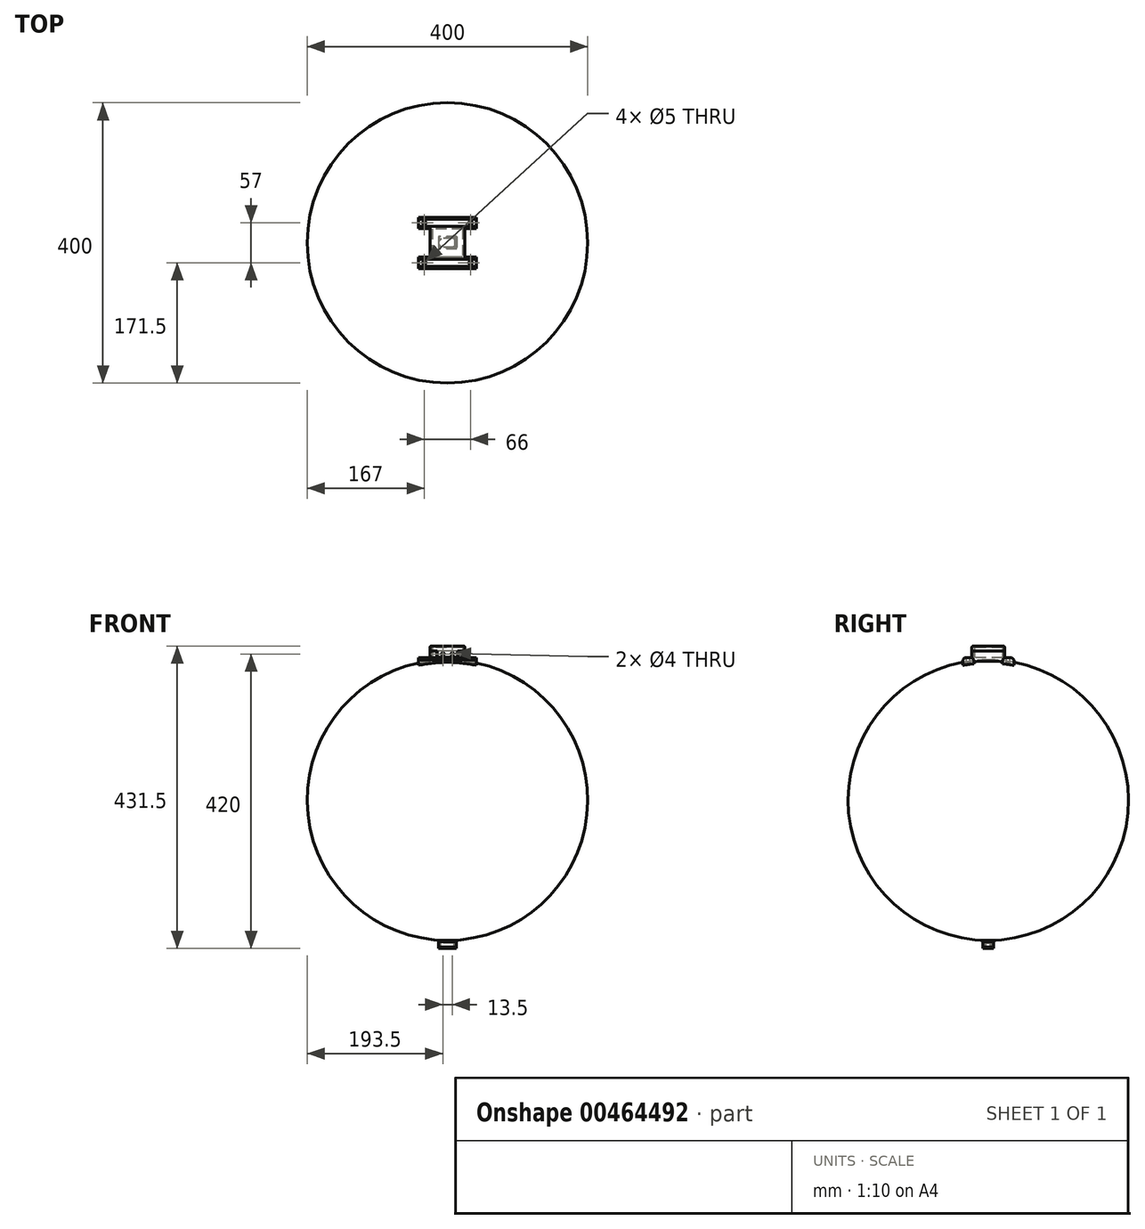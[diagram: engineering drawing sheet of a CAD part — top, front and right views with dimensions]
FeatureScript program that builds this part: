
annotation { "Feature Type Name" : "Feature", "Feature Type Description" : "" }
export const myFeature = defineFeature(function(context is Context, id is Id, definition is map)
    precondition{}
    {
        {
            assignVariable(context, id + "F0", {"name" : "R", "anyValue" : 200});
        }
        {
            assignVariable(context, id + "F1", {"name" : "T", "anyValue" : 3});
        }
        {
            assignVariable(context, id + "F2", {"name" : "t", "anyValue" : 2});
        }
        {
            var Q0;
            Q0=qCreatedBy(makeId("Right.planeOp"),FACE);
            var sketch = newSketch(context, id + "F3", { "sketchPlane" : qUnion([Q0])});
            skArc(sketch, "E0", {"start": v(0, -200) * mm, "mid": v(200, 0) * mm, "end": v(0, 200) * mm});
            skLineSegment(sketch, "E1", {"start": v(0, 133.29) * mm, "end": v(0, -166.2) * mm, "construction": true});
            skLineSegment(sketch, "E2", {"start": v(0, 200) * mm, "end": v(0, -200) * mm});
            skSolve(sketch);
        }
        {
            var Q0;
            Q0=makeQuery(id+"F3.imprint","IMPRINT",FACE,{"disambiguationData":[TD([[makeQuery(id+"F3.imprint","IMPRINT",EDGE,{"derivedFrom":sQuery(id+"F3.wireOp",EDGE,"E0")}),1.0]])]});
            var Q1;
            Q1=sQuery(id+"F3.wireOp",EDGE,"E1");
            revolve(context, id + "F4", {"entities" : qUnion([Q0]), "axis" : qUnion([Q1]), "revolveType" : RevolveType.FULL});
        }
        {
            var Q0;
            Q0=qCreatedBy(makeId("Top.planeOp"),FACE);
            cPlane(context, id + "F5", {"entities" : qUnion([Q0]), "cplaneType" : CPlaneType.OFFSET, "offset" : (getVariable(context, 'R') + getVariable(context, 'T')) * mm, "width" : 150 * mm, "height" : 150 * mm});
        }
        {
            var Q0;
            Q0=qCreatedBy(id+"F5.planeOp",FACE);
            var sketch = newSketch(context, id + "F6", { "sketchPlane" : qUnion([Q0])});
            skLineSegment(sketch, "E3.bottom", {"start": v(25, 36.5) * mm, "end": v(-25, 36.5) * mm});
            skLineSegment(sketch, "E3.top", {"start": v(25, -36.5) * mm, "end": v(-25, -36.5) * mm});
            skLineSegment(sketch, "E3.left", {"start": v(25, 20.5) * mm, "end": v(25, -20.5) * mm});
            skLineSegment(sketch, "E3.right", {"start": v(-25, 20.5) * mm, "end": v(-25, -20.5) * mm});
            skPoint(sketch, "E3.middle", {"position": v(0, 0) * mm});
            skLineSegment(sketch, "E4.bottom", {"start": v(-25, 36.5) * mm, "end": v(-41, 36.5) * mm});
            skLineSegment(sketch, "E4.top", {"start": v(-25, 20.5) * mm, "end": v(-41, 20.5) * mm});
            skLineSegment(sketch, "E4.right", {"start": v(-41, 36.5) * mm, "end": v(-41, 20.5) * mm});
            skLineSegment(sketch, "E5", {"start": v(0, 40.93) * mm, "end": v(0, -41.3) * mm, "construction": true});
            skLineSegment(sketch, "E6", {"start": v(40.69, 0) * mm, "end": v(-40.56, 0) * mm, "construction": true});
            skLineSegment(sketch, "E7.MirrorCS", {"start": v(25, 20.5) * mm, "end": v(41, 20.5) * mm});
            skLineSegment(sketch, "E8.MirrorCS", {"start": v(41, 36.5) * mm, "end": v(41, 20.5) * mm});
            skLineSegment(sketch, "E9.MirrorCS", {"start": v(25, 36.5) * mm, "end": v(41, 36.5) * mm});
            skLineSegment(sketch, "E10.MirrorCS", {"start": v(-25, -20.5) * mm, "end": v(-41, -20.5) * mm});
            skLineSegment(sketch, "E11.MirrorCS", {"start": v(-41, -36.5) * mm, "end": v(-41, -20.5) * mm});
            skLineSegment(sketch, "E12.MirrorCS", {"start": v(-25, -36.5) * mm, "end": v(-41, -36.5) * mm});
            skLineSegment(sketch, "E13.MirrorCS", {"start": v(25, -36.5) * mm, "end": v(41, -36.5) * mm});
            skLineSegment(sketch, "E14.MirrorCS", {"start": v(41, -36.5) * mm, "end": v(41, -20.5) * mm});
            skLineSegment(sketch, "E15.MirrorCS", {"start": v(25, -20.5) * mm, "end": v(41, -20.5) * mm});
            skLineSegment(sketch, "E16", {"start": v(-25, 20.5) * mm, "end": v(-41, 36.5) * mm, "construction": true});
            skLineSegment(sketch, "E17", {"start": v(-25, 36.5) * mm, "end": v(-41, 20.5) * mm, "construction": true});
            skCircle(sketch, "E18", {"center": v(-33, 28.5) * mm, "radius": 2.5 * mm});
            skCircle(sketch, "E19.MirrorC", {"center": v(33, 28.5) * mm, "radius": 2.5 * mm});
            skCircle(sketch, "E20.MirrorC", {"center": v(-33, -28.5) * mm, "radius": 2.5 * mm});
            skCircle(sketch, "E21.MirrorC", {"center": v(33, -28.5) * mm, "radius": 2.5 * mm});
            skSolve(sketch);
        }
        {
            var Q0;
            Q0 = qSketchRegion(id + "F6", true);
            var Q1;
            Q1=makeQuery(id+"F4.opRevolve","SWEPT_FACE",FACE,{"disambiguationData":[OSD([sQuery(id+"F3.wireOp",EDGE,"E0")])]});
            extrude(context, id + "F7", {"entities" : qUnion([Q0]), "endBound" : BoundingType.UP_TO_SURFACE, "oppositeDirection" : true, "depth" : 25 * mm, "endBoundEntityFace" : qUnion([Q1]), "offsetDistance" : 25 * mm});
        }
        {
            var Q0;
            Q0=makeQuery(id+"F7.opExtrude","CAP_EDGE",EDGE,{"disambiguationData":[OSD([sQuery(id+"F6.wireOp",EDGE,"E3.bottom"),sQuery(id+"F6.wireOp",EDGE,"E4.bottom"),sQuery(id+"F6.wireOp",EDGE,"E9.MirrorCS")])],"isStart":true});
            var Q1;
            Q1=makeQuery(id+"F7.opExtrude","CAP_EDGE",EDGE,{"disambiguationData":[OSD([sQuery(id+"F6.wireOp",EDGE,"E3.top"),sQuery(id+"F6.wireOp",EDGE,"E12.MirrorCS"),sQuery(id+"F6.wireOp",EDGE,"E13.MirrorCS")])],"isStart":true});
            var Q2;
            Q2=makeQuery(id+"F7.opExtrude","CAP_EDGE",EDGE,{"disambiguationData":[OSD([sQuery(id+"F6.wireOp",EDGE,"E4.top")])],"isStart":true});
            var Q3;
            Q3=makeQuery(id+"F7.opExtrude","CAP_EDGE",EDGE,{"disambiguationData":[OSD([sQuery(id+"F6.wireOp",EDGE,"E7.MirrorCS")])],"isStart":true});
            var Q4;
            Q4=makeQuery(id+"F7.opExtrude","CAP_EDGE",EDGE,{"disambiguationData":[OSD([sQuery(id+"F6.wireOp",EDGE,"E15.MirrorCS")])],"isStart":true});
            var Q5;
            Q5=makeQuery(id+"F7.opExtrude","CAP_EDGE",EDGE,{"disambiguationData":[OSD([sQuery(id+"F6.wireOp",EDGE,"E10.MirrorCS")])],"isStart":true});
            chamfer(context, id + "F8", {"entities" : qUnion([Q0, Q1, Q2, Q3, Q4, Q5]), "width" : 3 * mm, "tangentPropagation" : true});
        }
        {
            var Q0;
            Q0=makeQuery(id+"F7.opExtrude","CAP_FACE",FACE,{"disambiguationData":[OSD([sQuery(id+"F6.wireOp",EDGE,"E3.bottom"),sQuery(id+"F6.wireOp",EDGE,"E3.top"),sQuery(id+"F6.wireOp",EDGE,"E3.left"),sQuery(id+"F6.wireOp",EDGE,"E3.right"),sQuery(id+"F6.wireOp",EDGE,"E4.bottom"),sQuery(id+"F6.wireOp",EDGE,"E4.top"),sQuery(id+"F6.wireOp",EDGE,"E4.right"),sQuery(id+"F6.wireOp",EDGE,"E7.MirrorCS"),sQuery(id+"F6.wireOp",EDGE,"E8.MirrorCS"),sQuery(id+"F6.wireOp",EDGE,"E9.MirrorCS"),sQuery(id+"F6.wireOp",EDGE,"E10.MirrorCS"),sQuery(id+"F6.wireOp",EDGE,"E11.MirrorCS"),sQuery(id+"F6.wireOp",EDGE,"E12.MirrorCS"),sQuery(id+"F6.wireOp",EDGE,"E13.MirrorCS"),sQuery(id+"F6.wireOp",EDGE,"E14.MirrorCS"),sQuery(id+"F6.wireOp",EDGE,"E15.MirrorCS"),sQuery(id+"F6.wireOp",EDGE,"E18"),sQuery(id+"F6.wireOp",EDGE,"E19.MirrorC"),sQuery(id+"F6.wireOp",EDGE,"E20.MirrorC"),sQuery(id+"F6.wireOp",EDGE,"E21.MirrorC")])],"isStart":true});
            var sketch = newSketch(context, id + "F9", { "sketchPlane" : qUnion([Q0])});
            skLineSegment(sketch, "E22.bottom", {"start": v(25, 23.5) * mm, "end": v(-25, 23.5) * mm});
            skLineSegment(sketch, "E22.top", {"start": v(25, -23.5) * mm, "end": v(15, -23.5) * mm});
            skLineSegment(sketch, "E22.left", {"start": v(25, 23.5) * mm, "end": v(25, -23.5) * mm});
            skLineSegment(sketch, "E22.right", {"start": v(-25, 23.5) * mm, "end": v(-25, -23.5) * mm});
            skPoint(sketch, "E22.middle", {"position": v(0, 0) * mm});
            skLineSegment(sketch, "E23.0", {"start": v(21.5, 20) * mm, "end": v(-21.5, 20) * mm});
            skLineSegment(sketch, "E23.1", {"start": v(21.5, 20) * mm, "end": v(21.5, -20) * mm});
            skLineSegment(sketch, "E23.2", {"start": v(21.5, -20) * mm, "end": v(15, -20) * mm});
            skLineSegment(sketch, "E23.3", {"start": v(-21.5, 20) * mm, "end": v(-21.5, -20) * mm});
            skLineSegment(sketch, "E24", {"start": v(-15, -20) * mm, "end": v(-15, -23.5) * mm});
            skLineSegment(sketch, "E25", {"start": v(15, -20) * mm, "end": v(15, -23.5) * mm});
            skLineSegment(sketch, "E26.trimOffspring", {"start": v(-15, -20) * mm, "end": v(-21.5, -20) * mm});
            skLineSegment(sketch, "E27.trimOffspring", {"start": v(-15, -23.5) * mm, "end": v(-25, -23.5) * mm});
            skSolve(sketch);
        }
        {
            var Q0;
            Q0 = qSketchRegion(id + "F9", true);
            extrude(context, id + "F10", {"entities" : qUnion([Q0]), "operationType" : NewBodyOperationType.ADD, "depth" : 10 * mm, "offsetDistance" : 25 * mm});
        }
        {
            var Q0;
            Q0=makeQuery(id+"F10.opExtrude","CAP_FACE",FACE,{"disambiguationData":[OSD([sQuery(id+"F9.wireOp",EDGE,"E22.bottom"),sQuery(id+"F9.wireOp",EDGE,"E22.top"),sQuery(id+"F9.wireOp",EDGE,"E22.left"),sQuery(id+"F9.wireOp",EDGE,"E22.right"),sQuery(id+"F9.wireOp",EDGE,"E23.0"),sQuery(id+"F9.wireOp",EDGE,"E23.1"),sQuery(id+"F9.wireOp",EDGE,"E23.2"),sQuery(id+"F9.wireOp",EDGE,"E23.3"),sQuery(id+"F9.wireOp",EDGE,"E24"),sQuery(id+"F9.wireOp",EDGE,"E25"),sQuery(id+"F9.wireOp",EDGE,"E26.trimOffspring"),sQuery(id+"F9.wireOp",EDGE,"E27.trimOffspring")])],"isStart":false});
            var sketch = newSketch(context, id + "F11", { "sketchPlane" : qUnion([Q0])});
            skLineSegment(sketch, "E28.bottom", {"start": v(25, 23.5) * mm, "end": v(-25, 23.5) * mm});
            skLineSegment(sketch, "E28.top", {"start": v(25, -23.5) * mm, "end": v(-25, -23.5) * mm});
            skLineSegment(sketch, "E28.left", {"start": v(25, 23.5) * mm, "end": v(25, -23.5) * mm});
            skLineSegment(sketch, "E28.right", {"start": v(-25, 23.5) * mm, "end": v(-25, -23.5) * mm});
            skPoint(sketch, "E28.middle", {"position": v(0, 0) * mm});
            skLineSegment(sketch, "E29.0", {"start": v(21.5, 20) * mm, "end": v(-21.5, 20) * mm});
            skLineSegment(sketch, "E29.1", {"start": v(21.5, 20) * mm, "end": v(21.5, -20) * mm});
            skLineSegment(sketch, "E29.2", {"start": v(21.5, -20) * mm, "end": v(-21.5, -20) * mm});
            skLineSegment(sketch, "E29.3", {"start": v(-21.5, 20) * mm, "end": v(-21.5, -20) * mm});
            skSolve(sketch);
        }
        {
            var Q0;
            Q0 = qSketchRegion(id + "F11", true);
            extrude(context, id + "F12", {"entities" : qUnion([Q0]), "depth" : 5 * mm, "offsetDistance" : 25 * mm});
        }
        {
            var Q0;
            Q0=makeQuery(id+"F12.opExtrude","CAP_FACE",FACE,{"disambiguationData":[OSD([sQuery(id+"F11.wireOp",EDGE,"E28.bottom"),sQuery(id+"F11.wireOp",EDGE,"E28.top"),sQuery(id+"F11.wireOp",EDGE,"E28.left"),sQuery(id+"F11.wireOp",EDGE,"E28.right"),sQuery(id+"F11.wireOp",EDGE,"E29.0"),sQuery(id+"F11.wireOp",EDGE,"E29.1"),sQuery(id+"F11.wireOp",EDGE,"E29.2"),sQuery(id+"F11.wireOp",EDGE,"E29.3")])],"isStart":false});
            var sketch = newSketch(context, id + "F13", { "sketchPlane" : qUnion([Q0])});
            skLineSegment(sketch, "E30.bottom", {"start": v(25, 23.5) * mm, "end": v(-25, 23.5) * mm});
            skLineSegment(sketch, "E30.top", {"start": v(25, -23.5) * mm, "end": v(-25, -23.5) * mm});
            skLineSegment(sketch, "E30.left", {"start": v(25, 23.5) * mm, "end": v(25, -23.5) * mm});
            skLineSegment(sketch, "E30.right", {"start": v(-25, 23.5) * mm, "end": v(-25, -23.5) * mm});
            skPoint(sketch, "E30.middle", {"position": v(0, 0) * mm});
            skSolve(sketch);
        }
        {
            var Q0;
            Q0 = qSketchRegion(id + "F13", true);
            extrude(context, id + "F14", {"entities" : qUnion([Q0]), "operationType" : NewBodyOperationType.ADD, "depth" : 2 * mm, "offsetDistance" : 25 * mm});
        }
        {
            var Q0;
            Q0=makeQuery(id+"F14.opExtrude","CAP_FACE",FACE,{"disambiguationData":[OSD([sQuery(id+"F13.wireOp",EDGE,"E30.bottom"),sQuery(id+"F13.wireOp",EDGE,"E30.top"),sQuery(id+"F13.wireOp",EDGE,"E30.left"),sQuery(id+"F13.wireOp",EDGE,"E30.right")])],"isStart":false});
            var Q1;
            Q1=makeQuery(id+"F14.boolean.opBoolean","MERGE",EDGE,{"derivedFrom":[makeQuery(id+"F12.opExtrude","SWEPT_EDGE",EDGE,{"disambiguationData":[OSD([sQuery(id+"F11.wireOp",EDGE,"E28.top"),sQuery(id+"F11.wireOp",EDGE,"E28.right")])]}),makeQuery(id+"F14.opExtrude","SWEPT_EDGE",EDGE,{"disambiguationData":[OSD([sQuery(id+"F13.wireOp",EDGE,"E30.top"),sQuery(id+"F13.wireOp",EDGE,"E30.right")])]})]});
            var Q2;
            Q2=makeQuery(id+"F10.opExtrude","SWEPT_EDGE",EDGE,{"disambiguationData":[OSD([sQuery(id+"F6.wireOp",EDGE,"E3.bottom"),sQuery(id+"F6.wireOp",EDGE,"E3.top"),sQuery(id+"F6.wireOp",EDGE,"E3.left"),sQuery(id+"F6.wireOp",EDGE,"E3.right"),sQuery(id+"F6.wireOp",EDGE,"E4.bottom"),sQuery(id+"F6.wireOp",EDGE,"E4.top"),sQuery(id+"F6.wireOp",EDGE,"E4.right"),sQuery(id+"F6.wireOp",EDGE,"E7.MirrorCS"),sQuery(id+"F6.wireOp",EDGE,"E8.MirrorCS"),sQuery(id+"F6.wireOp",EDGE,"E9.MirrorCS"),sQuery(id+"F6.wireOp",EDGE,"E10.MirrorCS"),sQuery(id+"F6.wireOp",EDGE,"E11.MirrorCS"),sQuery(id+"F6.wireOp",EDGE,"E12.MirrorCS"),sQuery(id+"F6.wireOp",EDGE,"E13.MirrorCS"),sQuery(id+"F6.wireOp",EDGE,"E14.MirrorCS"),sQuery(id+"F6.wireOp",EDGE,"E15.MirrorCS"),sQuery(id+"F6.wireOp",EDGE,"E18"),sQuery(id+"F6.wireOp",EDGE,"E19.MirrorC"),sQuery(id+"F6.wireOp",EDGE,"E20.MirrorC"),sQuery(id+"F6.wireOp",EDGE,"E21.MirrorC"),sQuery(id+"F9.wireOp",EDGE,"E22.right"),sQuery(id+"F9.wireOp",EDGE,"E27.trimOffspring")])]});
            var Q3;
            Q3=makeQuery(id+"F10.opExtrude","SWEPT_EDGE",EDGE,{"disambiguationData":[OSD([sQuery(id+"F6.wireOp",EDGE,"E3.bottom"),sQuery(id+"F6.wireOp",EDGE,"E3.top"),sQuery(id+"F6.wireOp",EDGE,"E3.left"),sQuery(id+"F6.wireOp",EDGE,"E3.right"),sQuery(id+"F6.wireOp",EDGE,"E4.bottom"),sQuery(id+"F6.wireOp",EDGE,"E4.top"),sQuery(id+"F6.wireOp",EDGE,"E4.right"),sQuery(id+"F6.wireOp",EDGE,"E7.MirrorCS"),sQuery(id+"F6.wireOp",EDGE,"E8.MirrorCS"),sQuery(id+"F6.wireOp",EDGE,"E9.MirrorCS"),sQuery(id+"F6.wireOp",EDGE,"E10.MirrorCS"),sQuery(id+"F6.wireOp",EDGE,"E11.MirrorCS"),sQuery(id+"F6.wireOp",EDGE,"E12.MirrorCS"),sQuery(id+"F6.wireOp",EDGE,"E13.MirrorCS"),sQuery(id+"F6.wireOp",EDGE,"E14.MirrorCS"),sQuery(id+"F6.wireOp",EDGE,"E15.MirrorCS"),sQuery(id+"F6.wireOp",EDGE,"E18"),sQuery(id+"F6.wireOp",EDGE,"E19.MirrorC"),sQuery(id+"F6.wireOp",EDGE,"E20.MirrorC"),sQuery(id+"F6.wireOp",EDGE,"E21.MirrorC"),sQuery(id+"F9.wireOp",EDGE,"E22.bottom"),sQuery(id+"F9.wireOp",EDGE,"E22.right")])]});
            var Q4;
            Q4=makeQuery(id+"F14.boolean.opBoolean","MERGE",EDGE,{"derivedFrom":[makeQuery(id+"F12.opExtrude","SWEPT_EDGE",EDGE,{"disambiguationData":[OSD([sQuery(id+"F11.wireOp",EDGE,"E28.bottom"),sQuery(id+"F11.wireOp",EDGE,"E28.right")])]}),makeQuery(id+"F14.opExtrude","SWEPT_EDGE",EDGE,{"disambiguationData":[OSD([sQuery(id+"F13.wireOp",EDGE,"E30.bottom"),sQuery(id+"F13.wireOp",EDGE,"E30.right")])]})]});
            var Q5;
            Q5=makeQuery(id+"F10.opExtrude","SWEPT_EDGE",EDGE,{"disambiguationData":[OSD([sQuery(id+"F6.wireOp",EDGE,"E3.bottom"),sQuery(id+"F6.wireOp",EDGE,"E3.top"),sQuery(id+"F6.wireOp",EDGE,"E3.left"),sQuery(id+"F6.wireOp",EDGE,"E3.right"),sQuery(id+"F6.wireOp",EDGE,"E4.bottom"),sQuery(id+"F6.wireOp",EDGE,"E4.top"),sQuery(id+"F6.wireOp",EDGE,"E4.right"),sQuery(id+"F6.wireOp",EDGE,"E7.MirrorCS"),sQuery(id+"F6.wireOp",EDGE,"E8.MirrorCS"),sQuery(id+"F6.wireOp",EDGE,"E9.MirrorCS"),sQuery(id+"F6.wireOp",EDGE,"E10.MirrorCS"),sQuery(id+"F6.wireOp",EDGE,"E11.MirrorCS"),sQuery(id+"F6.wireOp",EDGE,"E12.MirrorCS"),sQuery(id+"F6.wireOp",EDGE,"E13.MirrorCS"),sQuery(id+"F6.wireOp",EDGE,"E14.MirrorCS"),sQuery(id+"F6.wireOp",EDGE,"E15.MirrorCS"),sQuery(id+"F6.wireOp",EDGE,"E18"),sQuery(id+"F6.wireOp",EDGE,"E19.MirrorC"),sQuery(id+"F6.wireOp",EDGE,"E20.MirrorC"),sQuery(id+"F6.wireOp",EDGE,"E21.MirrorC"),sQuery(id+"F9.wireOp",EDGE,"E22.top"),sQuery(id+"F9.wireOp",EDGE,"E22.left")])]});
            var Q6;
            Q6=makeQuery(id+"F14.boolean.opBoolean","MERGE",EDGE,{"derivedFrom":[makeQuery(id+"F12.opExtrude","SWEPT_EDGE",EDGE,{"disambiguationData":[OSD([sQuery(id+"F11.wireOp",EDGE,"E28.top"),sQuery(id+"F11.wireOp",EDGE,"E28.left")])]}),makeQuery(id+"F14.opExtrude","SWEPT_EDGE",EDGE,{"disambiguationData":[OSD([sQuery(id+"F13.wireOp",EDGE,"E30.top"),sQuery(id+"F13.wireOp",EDGE,"E30.left")])]})]});
            var Q7;
            Q7=makeQuery(id+"F10.opExtrude","SWEPT_EDGE",EDGE,{"disambiguationData":[OSD([sQuery(id+"F6.wireOp",EDGE,"E3.bottom"),sQuery(id+"F6.wireOp",EDGE,"E3.top"),sQuery(id+"F6.wireOp",EDGE,"E3.left"),sQuery(id+"F6.wireOp",EDGE,"E3.right"),sQuery(id+"F6.wireOp",EDGE,"E4.bottom"),sQuery(id+"F6.wireOp",EDGE,"E4.top"),sQuery(id+"F6.wireOp",EDGE,"E4.right"),sQuery(id+"F6.wireOp",EDGE,"E7.MirrorCS"),sQuery(id+"F6.wireOp",EDGE,"E8.MirrorCS"),sQuery(id+"F6.wireOp",EDGE,"E9.MirrorCS"),sQuery(id+"F6.wireOp",EDGE,"E10.MirrorCS"),sQuery(id+"F6.wireOp",EDGE,"E11.MirrorCS"),sQuery(id+"F6.wireOp",EDGE,"E12.MirrorCS"),sQuery(id+"F6.wireOp",EDGE,"E13.MirrorCS"),sQuery(id+"F6.wireOp",EDGE,"E14.MirrorCS"),sQuery(id+"F6.wireOp",EDGE,"E15.MirrorCS"),sQuery(id+"F6.wireOp",EDGE,"E18"),sQuery(id+"F6.wireOp",EDGE,"E19.MirrorC"),sQuery(id+"F6.wireOp",EDGE,"E20.MirrorC"),sQuery(id+"F6.wireOp",EDGE,"E21.MirrorC"),sQuery(id+"F9.wireOp",EDGE,"E22.bottom"),sQuery(id+"F9.wireOp",EDGE,"E22.left")])]});
            var Q8;
            Q8=makeQuery(id+"F14.boolean.opBoolean","MERGE",EDGE,{"derivedFrom":[makeQuery(id+"F12.opExtrude","SWEPT_EDGE",EDGE,{"disambiguationData":[OSD([sQuery(id+"F11.wireOp",EDGE,"E28.bottom"),sQuery(id+"F11.wireOp",EDGE,"E28.left")])]}),makeQuery(id+"F14.opExtrude","SWEPT_EDGE",EDGE,{"disambiguationData":[OSD([sQuery(id+"F13.wireOp",EDGE,"E30.bottom"),sQuery(id+"F13.wireOp",EDGE,"E30.left")])]})]});
            fillet(context, id + "F15", {"entities" : qUnion([Q0, Q1, Q2, Q3, Q4, Q5, Q6, Q7, Q8]), "radius" : 2.5 * mm, "tangentPropagation" : true, "allowEdgeOverflow" : false});
        }
        {
            var Q0;
            Q0=makeQuery(id+"F12.opExtrude","CAP_FACE",FACE,{"disambiguationData":[OSD([sQuery(id+"F11.wireOp",EDGE,"E28.bottom"),sQuery(id+"F11.wireOp",EDGE,"E28.top"),sQuery(id+"F11.wireOp",EDGE,"E28.left"),sQuery(id+"F11.wireOp",EDGE,"E28.right"),sQuery(id+"F11.wireOp",EDGE,"E29.0"),sQuery(id+"F11.wireOp",EDGE,"E29.1"),sQuery(id+"F11.wireOp",EDGE,"E29.2"),sQuery(id+"F11.wireOp",EDGE,"E29.3")])],"isStart":true});
            var sketch = newSketch(context, id + "F16", { "sketchPlane" : qUnion([Q0])});
            skLineSegment(sketch, "E31.bottom", {"start": v(-14.5, 23.5) * mm, "end": v(14.5, 23.5) * mm});
            skLineSegment(sketch, "E31.top", {"start": v(-14.5, 20) * mm, "end": v(14.5, 20) * mm});
            skLineSegment(sketch, "E31.left", {"start": v(-14.5, 23.5) * mm, "end": v(-14.5, 20) * mm});
            skLineSegment(sketch, "E31.right", {"start": v(14.5, 23.5) * mm, "end": v(14.5, 20) * mm});
            skSolve(sketch);
        }
        {
            var Q0;
            Q0 = qSketchRegion(id + "F16", true);
            extrude(context, id + "F17", {"entities" : qUnion([Q0]), "operationType" : NewBodyOperationType.ADD, "depth" : 9 * mm, "offsetDistance" : 25 * mm});
        }
        {
            var Q0;
            Q0=makeQuery(id+"F17.boolean.opBoolean","MERGE",FACE,{"derivedFrom":[makeQuery(id+"F14.boolean.opBoolean","MERGE",FACE,{"derivedFrom":[makeQuery(id+"F12.opExtrude","SWEPT_FACE",FACE,{"disambiguationData":[OSD([sQuery(id+"F11.wireOp",EDGE,"E28.top")])]}),makeQuery(id+"F14.opExtrude","SWEPT_FACE",FACE,{"disambiguationData":[OSD([sQuery(id+"F13.wireOp",EDGE,"E30.top")])]})]}),makeQuery(id+"F17.opExtrude","SWEPT_FACE",FACE,{"disambiguationData":[OSD([sQuery(id+"F16.wireOp",EDGE,"E31.bottom")])]})]});
            var sketch = newSketch(context, id + "F18", { "sketchPlane" : qUnion([Q0])});
            skCircle(sketch, "E32", {"center": v(-6.5, 208.5) * mm, "radius": 2 * mm});
            skCircle(sketch, "E33", {"center": v(7, 208.5) * mm, "radius": 2 * mm});
            skSolve(sketch);
        }
        {
            var Q0;
            Q0 = qSketchRegion(id + "F18", true);
            var Q1;
            Q1=makeQuery(id+"F17.boolean.opBoolean","MERGE",FACE,{"derivedFrom":[makeQuery(id+"F12.opExtrude","SWEPT_FACE",FACE,{"disambiguationData":[OSD([sQuery(id+"F11.wireOp",EDGE,"E29.2")])]}),makeQuery(id+"F17.opExtrude","SWEPT_FACE",FACE,{"disambiguationData":[OSD([sQuery(id+"F16.wireOp",EDGE,"E31.top")])]})]});
            extrude(context, id + "F19", {"entities" : qUnion([Q0]), "operationType" : NewBodyOperationType.REMOVE, "endBound" : BoundingType.UP_TO_SURFACE, "oppositeDirection" : true, "depth" : 25 * mm, "endBoundEntityFace" : qUnion([Q1]), "offsetDistance" : 25 * mm});
        }
        {
            var Q0;
            Q0=qCreatedBy(makeId("Top.planeOp"),FACE);
            cPlane(context, id + "F20", {"entities" : qUnion([Q0]), "cplaneType" : CPlaneType.OFFSET, "offset" : (getVariable(context, 'R') + getVariable(context, 't')) * mm, "oppositeDirection" : true, "width" : 150 * mm, "height" : 150 * mm});
        }
        {
            var Q0;
            Q0=qCreatedBy(id+"F20.planeOp",FACE);
            var sketch = newSketch(context, id + "F21", { "sketchPlane" : qUnion([Q0])});
            skLineSegment(sketch, "E34.bottom", {"start": v(12.5, 7.65) * mm, "end": v(-12.5, 7.65) * mm});
            skLineSegment(sketch, "E34.top", {"start": v(12.5, -7.65) * mm, "end": v(-12.5, -7.65) * mm});
            skLineSegment(sketch, "E34.left", {"start": v(12.5, 7.65) * mm, "end": v(12.5, -7.65) * mm});
            skLineSegment(sketch, "E34.right", {"start": v(-12.5, 7.65) * mm, "end": v(-12.5, -7.65) * mm});
            skPoint(sketch, "E34.middle", {"position": v(0, 0) * mm});
            skLineSegment(sketch, "E35.0", {"start": v(13.5, -8.65) * mm, "end": v(-12.5, -8.65) * mm});
            skLineSegment(sketch, "E35.1", {"start": v(13.5, 8.65) * mm, "end": v(13.5, -8.65) * mm});
            skLineSegment(sketch, "E35.2", {"start": v(13.5, 8.65) * mm, "end": v(-12.5, 8.65) * mm});
            skLineSegment(sketch, "E36", {"start": v(-12.5, -8.65) * mm, "end": v(-12.5, -7.65) * mm});
            skLineSegment(sketch, "E37", {"start": v(-12.5, 8.65) * mm, "end": v(-12.5, 7.65) * mm});
            skSolve(sketch);
        }
        {
            var Q0;
            Q0 = qSketchRegion(id + "F21", true);
            extrude(context, id + "F22", {"entities" : qUnion([Q0]), "depth" : 1 * mm, "offsetDistance" : 25 * mm});
        }
        {
            var Q0;
            Q0=makeQuery(id+"F21.imprint","IMPRINT",FACE,{"disambiguationData":[TD([[makeQuery(id+"F21.imprint","IMPRINT",EDGE,{"derivedFrom":sQuery(id+"F21.wireOp",EDGE,"E34.bottom")}),1.0]])]});
            extrude(context, id + "F23", {"entities" : qUnion([Q0]), "operationType" : NewBodyOperationType.ADD, "oppositeDirection" : true, "depth" : 1.5 * mm, "offsetDistance" : 25 * mm});
        }
        {
            var Q0;
            Q0=makeQuery(id+"F23.opExtrude","CAP_FACE",FACE,{"disambiguationData":[OSD([sQuery(id+"F21.wireOp",EDGE,"E34.bottom"),sQuery(id+"F21.wireOp",EDGE,"E34.top"),sQuery(id+"F21.wireOp",EDGE,"E34.left"),sQuery(id+"F21.wireOp",EDGE,"E34.right")])],"isStart":false});
            var sketch = newSketch(context, id + "F24", { "sketchPlane" : qUnion([Q0])});
            skLineSegment(sketch, "E38.bottom", {"start": v(12.5, 7.65) * mm, "end": v(-12.5, 7.65) * mm});
            skLineSegment(sketch, "E38.top", {"start": v(12.5, -7.65) * mm, "end": v(-12.5, -7.65) * mm});
            skLineSegment(sketch, "E38.left", {"start": v(12.5, 7.65) * mm, "end": v(12.5, -7.65) * mm});
            skLineSegment(sketch, "E38.right", {"start": v(-12.5, 7.65) * mm, "end": v(-12.5, 3) * mm});
            skPoint(sketch, "E38.middle", {"position": v(0, 0) * mm});
            skLineSegment(sketch, "E39.0", {"start": v(9.5, 6.15) * mm, "end": v(-9.5, 6.15) * mm});
            skLineSegment(sketch, "E39.1", {"start": v(11, 4.65) * mm, "end": v(11, -4.65) * mm});
            skLineSegment(sketch, "E39.2", {"start": v(9.5, -6.15) * mm, "end": v(-9.5, -6.15) * mm});
            skLineSegment(sketch, "E39.3", {"start": v(-11, 4.65) * mm, "end": v(-11, 3) * mm});
            skLineSegment(sketch, "E40.bottom", {"start": v(-12.5, 7.65) * mm, "end": v(-9.5, 7.65) * mm});
            skLineSegment(sketch, "E40.top", {"start": v(-11, 4.65) * mm, "end": v(-9.5, 4.65) * mm});
            skLineSegment(sketch, "E40.left", {"start": v(-12.5, 7.65) * mm, "end": v(-12.5, 4.65) * mm});
            skLineSegment(sketch, "E40.right", {"start": v(-9.5, 6.15) * mm, "end": v(-9.5, 4.65) * mm});
            skPoint(sketch, "E40.middle", {"position": v(-11, 6.15) * mm});
            skLineSegment(sketch, "E41.bottom", {"start": v(-12.5, -7.65) * mm, "end": v(-9.5, -7.65) * mm});
            skLineSegment(sketch, "E41.top", {"start": v(-11, -4.65) * mm, "end": v(-9.5, -4.65) * mm});
            skLineSegment(sketch, "E41.left", {"start": v(-12.5, -7.65) * mm, "end": v(-12.5, -4.65) * mm});
            skLineSegment(sketch, "E41.right", {"start": v(-9.5, -6.15) * mm, "end": v(-9.5, -4.65) * mm});
            skPoint(sketch, "E41.middle", {"position": v(-11, -6.15) * mm});
            skLineSegment(sketch, "E42.bottom", {"start": v(12.5, -7.65) * mm, "end": v(9.5, -7.65) * mm});
            skLineSegment(sketch, "E42.top", {"start": v(11, -4.65) * mm, "end": v(9.5, -4.65) * mm});
            skLineSegment(sketch, "E42.left", {"start": v(12.5, -7.65) * mm, "end": v(12.5, -4.65) * mm});
            skLineSegment(sketch, "E42.right", {"start": v(9.5, -6.15) * mm, "end": v(9.5, -4.65) * mm});
            skPoint(sketch, "E42.middle", {"position": v(11, -6.15) * mm});
            skLineSegment(sketch, "E43.bottom", {"start": v(12.5, 7.65) * mm, "end": v(9.5, 7.65) * mm});
            skLineSegment(sketch, "E43.top", {"start": v(11, 4.65) * mm, "end": v(9.5, 4.65) * mm});
            skLineSegment(sketch, "E43.left", {"start": v(12.5, 7.65) * mm, "end": v(12.5, 4.65) * mm});
            skLineSegment(sketch, "E43.right", {"start": v(9.5, 6.15) * mm, "end": v(9.5, 4.65) * mm});
            skPoint(sketch, "E43.middle", {"position": v(11, 6.15) * mm});
            skLineSegment(sketch, "E44", {"start": v(-11, 3) * mm, "end": v(-12.5, 3) * mm});
            skLineSegment(sketch, "E45", {"start": v(-12.5, -3) * mm, "end": v(-11, -3) * mm});
            skLineSegment(sketch, "E46.trimOffspring", {"start": v(-11, -3) * mm, "end": v(-11, -4.65) * mm});
            skLineSegment(sketch, "E47.trimOffspring", {"start": v(-12.5, -3) * mm, "end": v(-12.5, -7.65) * mm});
            skSolve(sketch);
        }
        {
            var Q0;
            Q0 = qSketchRegion(id + "F24", true);
            extrude(context, id + "F25", {"entities" : qUnion([Q0]), "operationType" : NewBodyOperationType.ADD, "depth" : 6 * mm, "offsetDistance" : 25 * mm});
        }
        {
            var Q0;
            Q0=makeQuery(id+"F25.opExtrude","CAP_FACE",FACE,{"disambiguationData":[OSD([sQuery(id+"F24.wireOp",EDGE,"E38.bottom"),sQuery(id+"F24.wireOp",EDGE,"E38.top"),sQuery(id+"F24.wireOp",EDGE,"E38.left"),sQuery(id+"F24.wireOp",EDGE,"E38.right"),sQuery(id+"F24.wireOp",EDGE,"E39.0"),sQuery(id+"F24.wireOp",EDGE,"E39.1"),sQuery(id+"F24.wireOp",EDGE,"E39.2"),sQuery(id+"F24.wireOp",EDGE,"E39.3"),sQuery(id+"F24.wireOp",EDGE,"E40.bottom"),sQuery(id+"F24.wireOp",EDGE,"E40.top"),sQuery(id+"F24.wireOp",EDGE,"E40.left"),sQuery(id+"F24.wireOp",EDGE,"E40.right"),sQuery(id+"F24.wireOp",EDGE,"E41.bottom"),sQuery(id+"F24.wireOp",EDGE,"E41.top"),sQuery(id+"F24.wireOp",EDGE,"E41.right"),sQuery(id+"F24.wireOp",EDGE,"E42.bottom"),sQuery(id+"F24.wireOp",EDGE,"E42.top"),sQuery(id+"F24.wireOp",EDGE,"E42.left"),sQuery(id+"F24.wireOp",EDGE,"E42.right"),sQuery(id+"F24.wireOp",EDGE,"E43.bottom"),sQuery(id+"F24.wireOp",EDGE,"E43.top"),sQuery(id+"F24.wireOp",EDGE,"E43.left"),sQuery(id+"F24.wireOp",EDGE,"E43.right"),sQuery(id+"F24.wireOp",EDGE,"E44"),sQuery(id+"F24.wireOp",EDGE,"E45"),sQuery(id+"F24.wireOp",EDGE,"E46.trimOffspring"),sQuery(id+"F24.wireOp",EDGE,"E47.trimOffspring")])],"isStart":false});
            var sketch = newSketch(context, id + "F26", { "sketchPlane" : qUnion([Q0])});
            skLineSegment(sketch, "E48.bottom", {"start": v(-12.5, 7.65) * mm, "end": v(12.5, 7.65) * mm});
            skLineSegment(sketch, "E48.top", {"start": v(-12.5, -7.65) * mm, "end": v(12.5, -7.65) * mm});
            skLineSegment(sketch, "E48.left", {"start": v(-12.5, 7.65) * mm, "end": v(-12.5, -7.65) * mm});
            skLineSegment(sketch, "E48.right", {"start": v(12.5, 7.65) * mm, "end": v(12.5, -7.65) * mm});
            skSolve(sketch);
        }
        {
            var Q0;
            Q0 = qSketchRegion(id + "F26", true);
            extrude(context, id + "F27", {"entities" : qUnion([Q0]), "depth" : 2 * mm, "offsetDistance" : 25 * mm});
        }
        {
            var Q0;
            Q0=makeQuery(id+"F27.opExtrude","CAP_FACE",FACE,{"disambiguationData":[OSD([sQuery(id+"F26.wireOp",EDGE,"E48.bottom"),sQuery(id+"F26.wireOp",EDGE,"E48.top"),sQuery(id+"F26.wireOp",EDGE,"E48.left"),sQuery(id+"F26.wireOp",EDGE,"E48.right")])],"isStart":false});
            var sketch = newSketch(context, id + "F28", { "sketchPlane" : qUnion([Q0])});
            skCircle(sketch, "E49", {"center": v(-11, 6.15) * mm, "radius": 0.5 * mm});
            skLineSegment(sketch, "E50", {"start": v(0, 7.65) * mm, "end": v(0, -7.65) * mm, "construction": true});
            skLineSegment(sketch, "E51", {"start": v(12.5, 0) * mm, "end": v(-12.5, 0) * mm, "construction": true});
            skCircle(sketch, "E52.MirrorC", {"center": v(-11, -6.15) * mm, "radius": 0.5 * mm});
            skCircle(sketch, "E53.MirrorC", {"center": v(11, 6.15) * mm, "radius": 0.5 * mm});
            skCircle(sketch, "E54.MirrorC", {"center": v(11, -6.15) * mm, "radius": 0.5 * mm});
            skSolve(sketch);
        }
        {
            var Q0;
            Q0 = qSketchRegion(id + "F28", true);
            var Q1;
            Q1=makeQuery(id+"F22.opExtrude","CAP_FACE",FACE,{"disambiguationData":[OSD([sQuery(id+"F21.wireOp",EDGE,"E34.right"),sQuery(id+"F21.wireOp",EDGE,"E35.0"),sQuery(id+"F21.wireOp",EDGE,"E35.1"),sQuery(id+"F21.wireOp",EDGE,"E35.2"),sQuery(id+"F21.wireOp",EDGE,"E36"),sQuery(id+"F21.wireOp",EDGE,"E37")])],"isStart":false});
            extrude(context, id + "F29", {"entities" : qUnion([Q0]), "operationType" : NewBodyOperationType.REMOVE, "endBound" : BoundingType.UP_TO_SURFACE, "oppositeDirection" : true, "depth" : 25 * mm, "endBoundEntityFace" : qUnion([Q1]), "offsetDistance" : 25 * mm});
        }
    });
